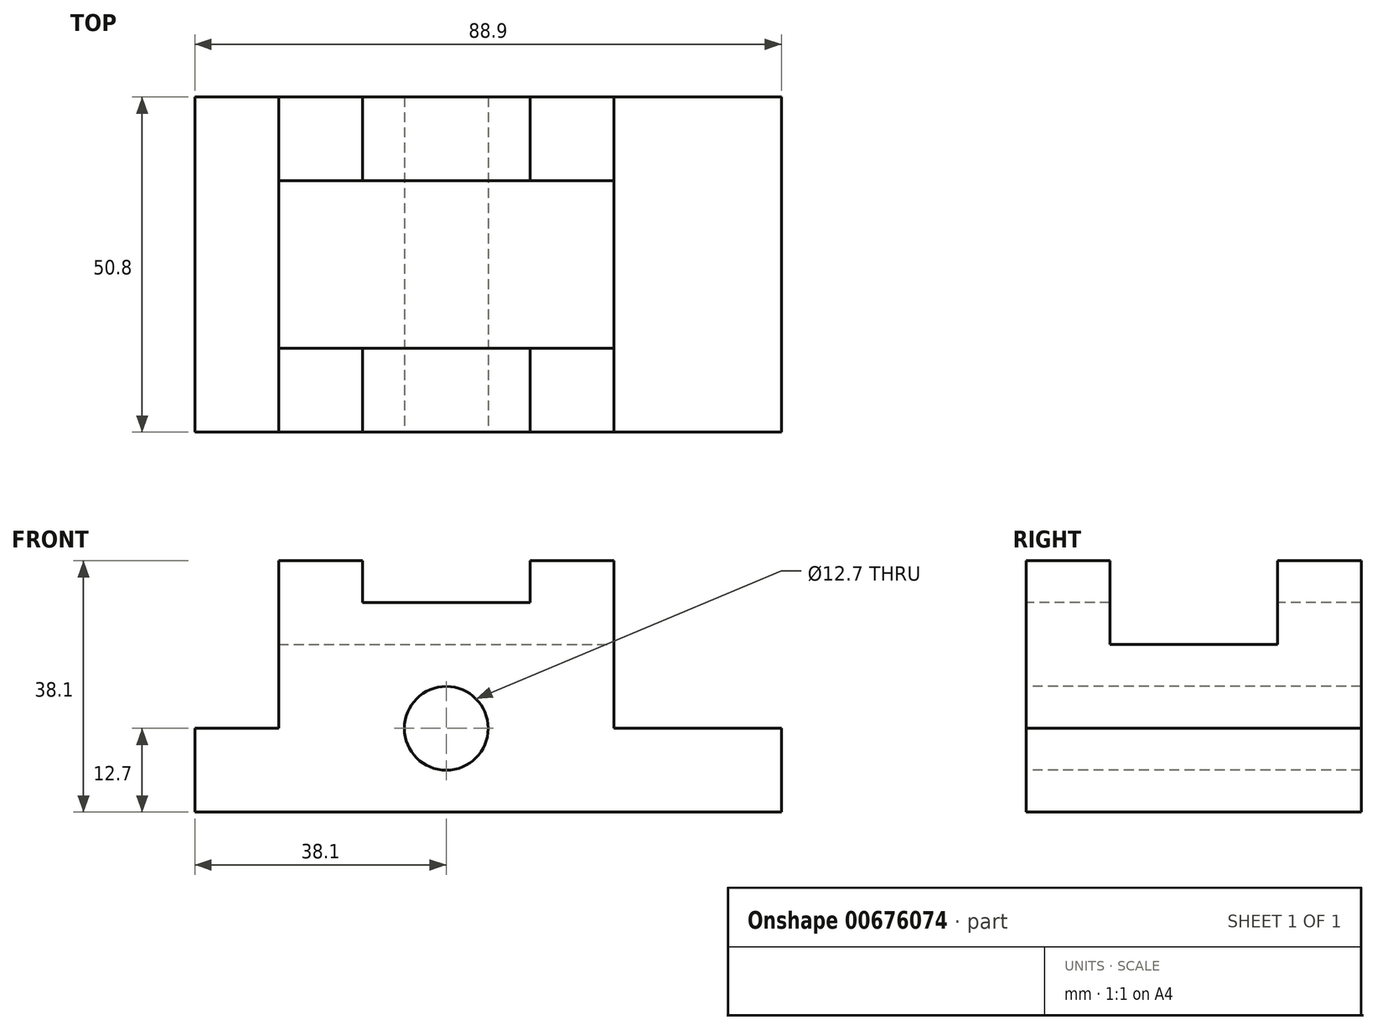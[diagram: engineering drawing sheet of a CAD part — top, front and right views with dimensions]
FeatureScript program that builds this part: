
annotation { "Feature Type Name" : "Feature", "Feature Type Description" : "" }
export const myFeature = defineFeature(function(context is Context, id is Id, definition is map)
    precondition{}
    {
        {
            var Q0;
            Q0=qCreatedBy(makeId("Front.planeOp"),FACE);
            var sketch = newSketch(context, id + "F0", { "sketchPlane" : qUnion([Q0])});
            skLineSegment(sketch, "E0.bottom", {"start": v(-44.45, 19.05) * mm, "end": v(44.45, 19.05) * mm});
            skLineSegment(sketch, "E0.top", {"start": v(-44.45, -19.05) * mm, "end": v(44.45, -19.05) * mm});
            skLineSegment(sketch, "E0.left", {"start": v(-44.45, 19.05) * mm, "end": v(-44.45, -19.05) * mm});
            skLineSegment(sketch, "E0.right", {"start": v(44.45, 19.05) * mm, "end": v(44.45, -19.05) * mm});
            skPoint(sketch, "E0.middle", {"position": v(0, 0) * mm});
            skSolve(sketch);
        }
        {
            var Q0;
            Q0=makeQuery(id+"F0.imprint","IMPRINT",FACE,{"disambiguationData":[TD([[makeQuery(id+"F0.imprint","IMPRINT",EDGE,{"derivedFrom":sQuery(id+"F0.wireOp",EDGE,"E0.bottom")}),-1.0]])]});
            extrude(context, id + "F1", {"entities" : qUnion([Q0]), "depth" : 50.8 * mm, "offsetDistance" : 25.4 * mm});
        }
        {
            var Q0;
            Q0=makeQuery(id+"F1.opExtrude","CAP_FACE",FACE,{"disambiguationData":[OSD([sQuery(id+"F0.wireOp",EDGE,"E0.bottom"),sQuery(id+"F0.wireOp",EDGE,"E0.top"),sQuery(id+"F0.wireOp",EDGE,"E0.left"),sQuery(id+"F0.wireOp",EDGE,"E0.right")])],"isStart":false});
            var sketch = newSketch(context, id + "F2", { "sketchPlane" : qUnion([Q0])});
            skLineSegment(sketch, "E1.bottom", {"start": v(-31.75, 19.05) * mm, "end": v(-44.45, 19.05) * mm});
            skLineSegment(sketch, "E1.top", {"start": v(-31.75, -6.35) * mm, "end": v(-44.45, -6.35) * mm});
            skLineSegment(sketch, "E1.left", {"start": v(-31.75, 19.05) * mm, "end": v(-31.75, -6.35) * mm});
            skLineSegment(sketch, "E1.right", {"start": v(-44.45, 19.05) * mm, "end": v(-44.45, -6.35) * mm});
            skLineSegment(sketch, "E2.bottom", {"start": v(19.05, 19.05) * mm, "end": v(44.45, 19.05) * mm});
            skLineSegment(sketch, "E2.top", {"start": v(19.05, -6.35) * mm, "end": v(44.45, -6.35) * mm});
            skLineSegment(sketch, "E2.left", {"start": v(19.05, 19.05) * mm, "end": v(19.05, -6.35) * mm});
            skLineSegment(sketch, "E2.right", {"start": v(44.45, 19.05) * mm, "end": v(44.45, -6.35) * mm});
            skLineSegment(sketch, "E3.bottom", {"start": v(-19.05, 19.05) * mm, "end": v(6.35, 19.05) * mm});
            skLineSegment(sketch, "E3.top", {"start": v(-19.05, 12.7) * mm, "end": v(6.35, 12.7) * mm});
            skLineSegment(sketch, "E3.left", {"start": v(-19.05, 19.05) * mm, "end": v(-19.05, 12.7) * mm});
            skLineSegment(sketch, "E3.right", {"start": v(6.35, 19.05) * mm, "end": v(6.35, 12.7) * mm});
            skCircle(sketch, "E4", {"center": v(-6.35, -6.35) * mm, "radius": 6.35 * mm});
            skSolve(sketch);
        }
        {
            var Q0;
            Q0=makeQuery(id+"F2.imprint","IMPRINT",FACE,{"disambiguationData":[TD([[makeQuery(id+"F2.imprint","IMPRINT",EDGE,{"derivedFrom":sQuery(id+"F2.wireOp",EDGE,"E1.bottom")}),-1.0]])]});
            extrude(context, id + "F3", {"entities" : qUnion([Q0]), "operationType" : NewBodyOperationType.REMOVE, "oppositeDirection" : true, "depth" : 50.8 * mm, "offsetDistance" : 25.4 * mm});
        }
        {
            var Q0;
            Q0=makeQuery(id+"F2.imprint","IMPRINT",FACE,{"disambiguationData":[TD([[makeQuery(id+"F2.imprint","IMPRINT",EDGE,{"derivedFrom":sQuery(id+"F2.wireOp",EDGE,"E3.bottom")}),-1.0]])]});
            extrude(context, id + "F4", {"entities" : qUnion([Q0]), "operationType" : NewBodyOperationType.REMOVE, "oppositeDirection" : true, "depth" : 50.8 * mm, "offsetDistance" : 25.4 * mm});
        }
        {
            var Q0;
            Q0=makeQuery(id+"F2.imprint","IMPRINT",FACE,{"disambiguationData":[TD([[makeQuery(id+"F2.imprint","IMPRINT",EDGE,{"derivedFrom":sQuery(id+"F2.wireOp",EDGE,"E4")}),1.0]])]});
            extrude(context, id + "F5", {"entities" : qUnion([Q0]), "operationType" : NewBodyOperationType.ADD, "depth" : 50.8 * mm, "offsetDistance" : 25.4 * mm});
        }
        {
            var Q0;
            Q0=makeQuery(id+"F5.opExtrude","CAP_FACE",FACE,{"disambiguationData":[OSD([sQuery(id+"F2.wireOp",EDGE,"E4")])],"isStart":false});
            extrude(context, id + "F6", {"entities" : qUnion([Q0]), "operationType" : NewBodyOperationType.REMOVE, "oppositeDirection" : true, "depth" : 50.8 * mm, "offsetDistance" : 25.4 * mm});
        }
        {
            var Q0;
            Q0=makeQuery(id+"F2.imprint","IMPRINT",FACE,{"disambiguationData":[TD([[makeQuery(id+"F2.imprint","IMPRINT",EDGE,{"derivedFrom":sQuery(id+"F2.wireOp",EDGE,"E4")}),1.0]])]});
            extrude(context, id + "F7", {"entities" : qUnion([Q0]), "operationType" : NewBodyOperationType.REMOVE, "oppositeDirection" : true, "depth" : 50.8 * mm, "offsetDistance" : 25.4 * mm});
        }
        {
            var Q0;
            Q0=makeQuery(id+"F2.imprint","IMPRINT",FACE,{"disambiguationData":[TD([[makeQuery(id+"F2.imprint","IMPRINT",EDGE,{"derivedFrom":sQuery(id+"F2.wireOp",EDGE,"E2.bottom")}),-1.0]])]});
            extrude(context, id + "F8", {"entities" : qUnion([Q0]), "operationType" : NewBodyOperationType.REMOVE, "oppositeDirection" : true, "depth" : 50.8 * mm, "offsetDistance" : 25.4 * mm});
        }
        {
            var Q0;
            Q0=makeQuery(id+"F8.boolean.opBoolean","COPY",FACE,{"derivedFrom":makeQuery(id+"F8.opExtrude","SWEPT_FACE",FACE,{"disambiguationData":[OSD([sQuery(id+"F2.wireOp",EDGE,"E2.left")])]})});
            var sketch = newSketch(context, id + "F9", { "sketchPlane" : qUnion([Q0])});
            skLineSegment(sketch, "E5.bottom", {"start": v(-38.1, 19.05) * mm, "end": v(-12.7, 19.05) * mm});
            skLineSegment(sketch, "E5.top", {"start": v(-38.1, 6.35) * mm, "end": v(-12.7, 6.35) * mm});
            skLineSegment(sketch, "E5.left", {"start": v(-38.1, 19.05) * mm, "end": v(-38.1, 6.35) * mm});
            skLineSegment(sketch, "E5.right", {"start": v(-12.7, 19.05) * mm, "end": v(-12.7, 6.35) * mm});
            skSolve(sketch);
        }
        {
            var Q0;
            Q0=makeQuery(id+"F9.imprint","IMPRINT",FACE,{"disambiguationData":[TD([[makeQuery(id+"F9.imprint","IMPRINT",EDGE,{"derivedFrom":sQuery(id+"F9.wireOp",EDGE,"E5.bottom")}),1.0]])]});
            extrude(context, id + "F10", {"entities" : qUnion([Q0]), "operationType" : NewBodyOperationType.REMOVE, "oppositeDirection" : true, "depth" : 50.8 * mm, "offsetDistance" : 25.4 * mm});
        }
    });
